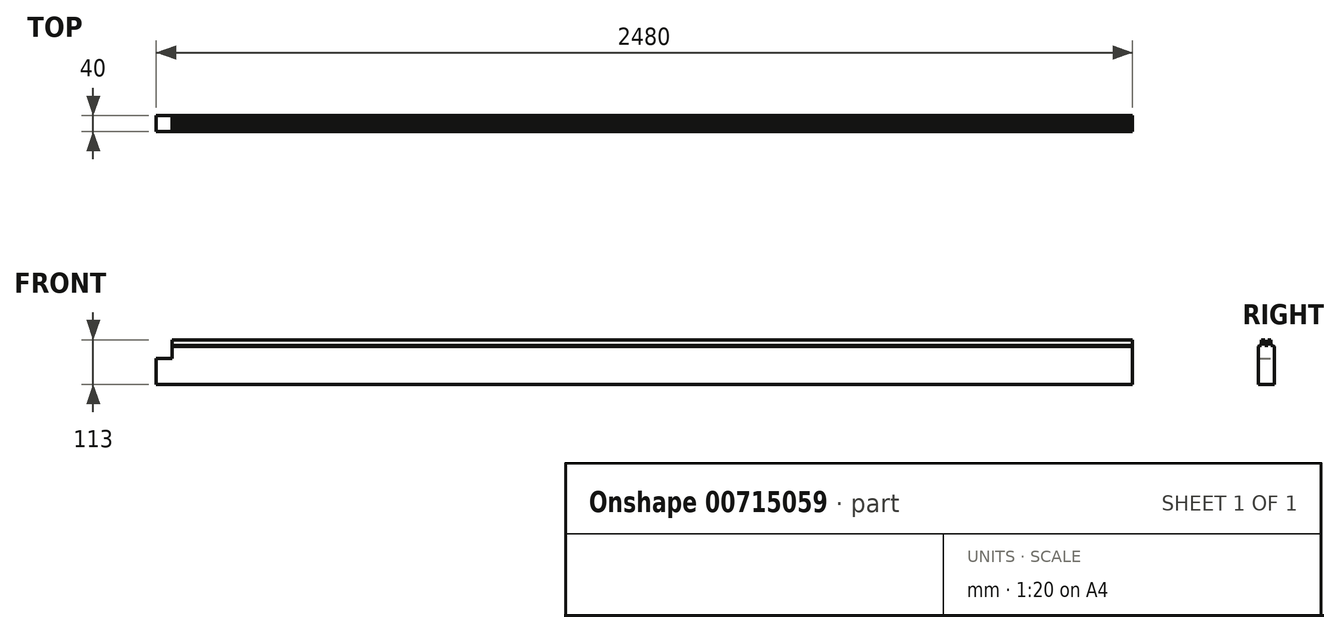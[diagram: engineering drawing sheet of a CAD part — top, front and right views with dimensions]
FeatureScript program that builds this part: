
annotation { "Feature Type Name" : "Feature", "Feature Type Description" : "" }
export const myFeature = defineFeature(function(context is Context, id is Id, definition is map)
    precondition{}
    {
        {
            assignVariable(context, id + "F0", {"name" : "Laenge", "anyValue" : 5100 - 1200 - 1420});
        }
        {
            var Q0;
            Q0=qCreatedBy(makeId("Right.planeOp"),FACE);
            var sketch = newSketch(context, id + "F1", { "sketchPlane" : qUnion([Q0])});
            skLineSegment(sketch, "E0", {"start": v(20, 63) * mm, "end": v(20, -63) * mm});
            skLineSegment(sketch, "E1", {"start": v(20, -63) * mm, "end": v(17, -66) * mm});
            skLineSegment(sketch, "E2", {"start": v(17, -66) * mm, "end": v(12, -66) * mm});
            skLineSegment(sketch, "E3", {"start": v(12, -52) * mm, "end": v(12, -66) * mm});
            skLineSegment(sketch, "E4", {"start": v(12, -52) * mm, "end": v(4, -52) * mm});
            skLineSegment(sketch, "E5", {"start": v(4, -66) * mm, "end": v(4, -52) * mm});
            skLineSegment(sketch, "E6", {"start": v(4, -66) * mm, "end": v(-4, -66) * mm});
            skLineSegment(sketch, "E7", {"start": v(-4, -52) * mm, "end": v(-4, -66) * mm});
            skLineSegment(sketch, "E8", {"start": v(-4, -52) * mm, "end": v(-12, -52) * mm});
            skLineSegment(sketch, "E9", {"start": v(-12, -66) * mm, "end": v(-12, -52) * mm});
            skLineSegment(sketch, "E10", {"start": v(-12, -66) * mm, "end": v(-17, -66) * mm});
            skLineSegment(sketch, "E11", {"start": v(-17, -66) * mm, "end": v(-20, -63) * mm});
            skLineSegment(sketch, "E12", {"start": v(-20, -63) * mm, "end": v(-20, 63) * mm});
            skLineSegment(sketch, "E13", {"start": v(-20, 63) * mm, "end": v(-17, 66) * mm});
            skLineSegment(sketch, "E14", {"start": v(-17, 66) * mm, "end": v(-12, 66) * mm});
            skLineSegment(sketch, "E15", {"start": v(-4, 66) * mm, "end": v(4, 66) * mm});
            skLineSegment(sketch, "E16", {"start": v(12, 66) * mm, "end": v(17, 66) * mm});
            skLineSegment(sketch, "E17", {"start": v(17, 66) * mm, "end": v(20, 63) * mm});
            skPoint(sketch, "E18.end.orphan", {"position": v(12, 57.8) * mm});
            skPoint(sketch, "E19.end.orphan", {"position": v(4, 66.3) * mm});
            skPoint(sketch, "E20.end.orphan", {"position": v(-4, 66.3) * mm});
            skLineSegment(sketch, "E21", {"start": v(-12, 66) * mm, "end": v(-12, 80) * mm});
            skLineSegment(sketch, "E22", {"start": v(-12, 80) * mm, "end": v(-4, 80) * mm});
            skLineSegment(sketch, "E23", {"start": v(-4, 80) * mm, "end": v(-4, 66) * mm});
            skLineSegment(sketch, "E24", {"start": v(4, 66) * mm, "end": v(4, 80) * mm});
            skLineSegment(sketch, "E25", {"start": v(4, 80) * mm, "end": v(12, 80) * mm});
            skLineSegment(sketch, "E26", {"start": v(12, 80) * mm, "end": v(12, 66) * mm});
            skLineSegment(sketch, "E27", {"start": v(20, -33) * mm, "end": v(-20, -33) * mm});
            skLineSegment(sketch, "E28", {"start": v(20, 33) * mm, "end": v(-20, 33) * mm});
            skPoint(sketch, "E29.end.orphan", {"position": v(-141.42, 0) * mm});
            skLineSegment(sketch, "E30", {"start": v(20, 0) * mm, "end": v(-20, 0) * mm});
            skLineSegment(sketch, "E31", {"start": v(20, 0) * mm, "end": v(-20, 0) * mm, "construction": true});
            skLineSegment(sketch, "E32", {"start": v(0, 33) * mm, "end": v(0, -33) * mm, "construction": true});
            skSolve(sketch);
        }
        {
            var Q0;
            Q0=qCreatedBy(makeId("Front.planeOp"),FACE);
            var sketch = newSketch(context, id + "F2", { "sketchPlane" : qUnion([Q0])});
            skLineSegment(sketch, "E33", {"start": v(1240, 0) * mm, "end": v(-1240, 0) * mm, "construction": true});
            skPoint(sketch, "E34.right.start.orphan", {"position": v(-259.12, 108.1) * mm});
            skPoint(sketch, "E35.left.start.orphan", {"position": v(237.35, 108.1) * mm});
            skPoint(sketch, "E36.left.end.orphan", {"position": v(237.35, -84.05) * mm});
            skPoint(sketch, "E36.bottom.start.orphan", {"position": v(237.35, -117.05) * mm});
            skPoint(sketch, "E37.right.start.orphan", {"position": v(-259.12, -117.05) * mm});
            skPoint(sketch, "E37.top.end.orphan", {"position": v(-259.12, -84.05) * mm});
            skLineSegment(sketch, "E38.bottom", {"start": v(-1280, 33) * mm, "end": v(-1200, 33) * mm});
            skLineSegment(sketch, "E38.top", {"start": v(-1280, 133) * mm, "end": v(-1200, 133) * mm});
            skLineSegment(sketch, "E38.left", {"start": v(-1280, 33) * mm, "end": v(-1280, 133) * mm});
            skLineSegment(sketch, "E38.right", {"start": v(-1200, 33) * mm, "end": v(-1200, 133) * mm});
            skPoint(sketch, "E38.middle", {"position": v(-1240, 83) * mm});
            skLineSegment(sketch, "E39.bottom", {"start": v(-1280, -133) * mm, "end": v(-1200, -133) * mm});
            skLineSegment(sketch, "E39.top", {"start": v(-1280, -33) * mm, "end": v(-1200, -33) * mm});
            skLineSegment(sketch, "E39.left", {"start": v(-1280, -133) * mm, "end": v(-1280, -33) * mm});
            skLineSegment(sketch, "E39.right", {"start": v(-1200, -133) * mm, "end": v(-1200, -33) * mm});
            skPoint(sketch, "E39.middle", {"position": v(-1240, -83) * mm});
            skLineSegment(sketch, "E40.bottom", {"start": v(1280, 33) * mm, "end": v(1200, 33) * mm});
            skLineSegment(sketch, "E40.top", {"start": v(1280, 133) * mm, "end": v(1200, 133) * mm});
            skLineSegment(sketch, "E40.left", {"start": v(1280, 33) * mm, "end": v(1280, 133) * mm});
            skLineSegment(sketch, "E40.right", {"start": v(1200, 33) * mm, "end": v(1200, 133) * mm});
            skPoint(sketch, "E40.middle", {"position": v(1240, 83) * mm});
            skLineSegment(sketch, "E41.bottom", {"start": v(1280, -33) * mm, "end": v(1200, -33) * mm});
            skLineSegment(sketch, "E41.top", {"start": v(1280, -133) * mm, "end": v(1200, -133) * mm});
            skLineSegment(sketch, "E41.left", {"start": v(1280, -33) * mm, "end": v(1280, -133) * mm});
            skLineSegment(sketch, "E41.right", {"start": v(1200, -33) * mm, "end": v(1200, -133) * mm});
            skPoint(sketch, "E41.middle", {"position": v(1240, -83) * mm});
            skSolve(sketch);
        }
        {
            var Q0;
            {var subQ3=sQuery(id+"F1.wireOp",EDGE,"E13");Q0=makeQuery(id+"F1.imprint","IMPRINT",FACE,{"disambiguationData":[TD([[makeQuery(id+"F1.imprint","IMPRINT",EDGE,{"derivedFrom":subQ3}),-1.0]])]});}
            var Q1;
            {var subQ0=sQuery(id+"F1.wireOp",EDGE,"E28");Q1=makeQuery(id+"F1.imprint","IMPRINT",FACE,{"disambiguationData":[TD([[makeQuery(id+"F1.imprint","IMPRINT",EDGE,{"derivedFrom":subQ0}),1.0]])]});}
            var Q2;
            {var subQ0=sQuery(id+"F1.wireOp",EDGE,"E27");Q2=makeQuery(id+"F1.imprint","IMPRINT",FACE,{"disambiguationData":[TD([[makeQuery(id+"F1.imprint","IMPRINT",EDGE,{"derivedFrom":subQ0}),-1.0]])]});}
            var Q3;
            {var subQ1=sQuery(id+"F1.wireOp",EDGE,"E1");Q3=makeQuery(id+"F1.imprint","IMPRINT",FACE,{"disambiguationData":[TD([[makeQuery(id+"F1.imprint","IMPRINT",EDGE,{"derivedFrom":subQ1}),-1.0]])]});}
            extrude(context, id + "F3", {"entities" : qUnion([Q0, Q1, Q2, Q3]), "endBound" : BoundingType.SYMMETRIC, "depth" : getVariable(context, 'Laenge') * mm, "offsetDistance" : 25 * mm});
        }
        {
            var Q0;
            Q0=makeQuery(id+"F2.imprint","IMPRINT",FACE,{"disambiguationData":[TD([[makeQuery(id+"F2.imprint","IMPRINT",EDGE,{"derivedFrom":sQuery(id+"F2.wireOp",EDGE,"E38.bottom")}),1.0]])]});
            var Q1;
            Q1=makeQuery(id+"F2.imprint","IMPRINT",FACE,{"disambiguationData":[TD([[makeQuery(id+"F2.imprint","IMPRINT",EDGE,{"derivedFrom":sQuery(id+"F2.wireOp",EDGE,"E39.bottom")}),1.0]])]});
            extrude(context, id + "F4", {"entities" : qUnion([Q0, Q1]), "operationType" : NewBodyOperationType.REMOVE, "endBound" : BoundingType.SYMMETRIC, "oppositeDirection" : true, "depth" : 50 * mm, "offsetDistance" : 25 * mm});
        }
        {
            var Q0;
            Q0=makeQuery(id+"F3.opExtrude","SWEPT_FACE",FACE,{"disambiguationData":[OSD([sQuery(id+"F1.wireOp",EDGE,"E12")])]});
            var sketch = newSketch(context, id + "F5", { "sketchPlane" : qUnion([Q0])});
            skLineSegment(sketch, "E42.bottom", {"start": v(-1240, -33) * mm, "end": v(1240, -33) * mm});
            skLineSegment(sketch, "E42.top", {"start": v(-1240, -83) * mm, "end": v(1240, -83) * mm});
            skLineSegment(sketch, "E42.left", {"start": v(-1240, -33) * mm, "end": v(-1240, -83) * mm});
            skLineSegment(sketch, "E42.right", {"start": v(1240, -33) * mm, "end": v(1240, -83) * mm});
            skSolve(sketch);
        }
        {
            var Q0;
            {var subQ1=sQuery(id+"F5.wireOp",EDGE,"E42.top");Q0=makeQuery(id+"F5.imprint","IMPRINT",FACE,{"disambiguationData":[TD([[makeQuery(id+"F5.imprint","IMPRINT",EDGE,{"derivedFrom":subQ1}),1.0]])]});}
            var Q1;
            {var subQ1=sQuery(id+"F1.wireOp",EDGE,"E12");var subQ5=makeQuery(id+"F3.opExtrude","SWEPT_EDGE",EDGE,{"disambiguationData":[OSD([sQuery(id+"F1.wireOp",EDGE,"E11"),subQ1])]});Q1=makeQuery(id+"F5.imprint","IMPRINT",FACE,{"disambiguationData":[TD([[makeQuery(id+"F5.imprint","IMPRINT",EDGE,{"derivedFrom":subQ5}),-1.0]])]});}
            extrude(context, id + "F6", {"entities" : qUnion([Q0, Q1]), "operationType" : NewBodyOperationType.REMOVE, "endBound" : BoundingType.UP_TO_NEXT, "oppositeDirection" : true, "depth" : 25 * mm, "offsetDistance" : 25 * mm});
        }
    });
